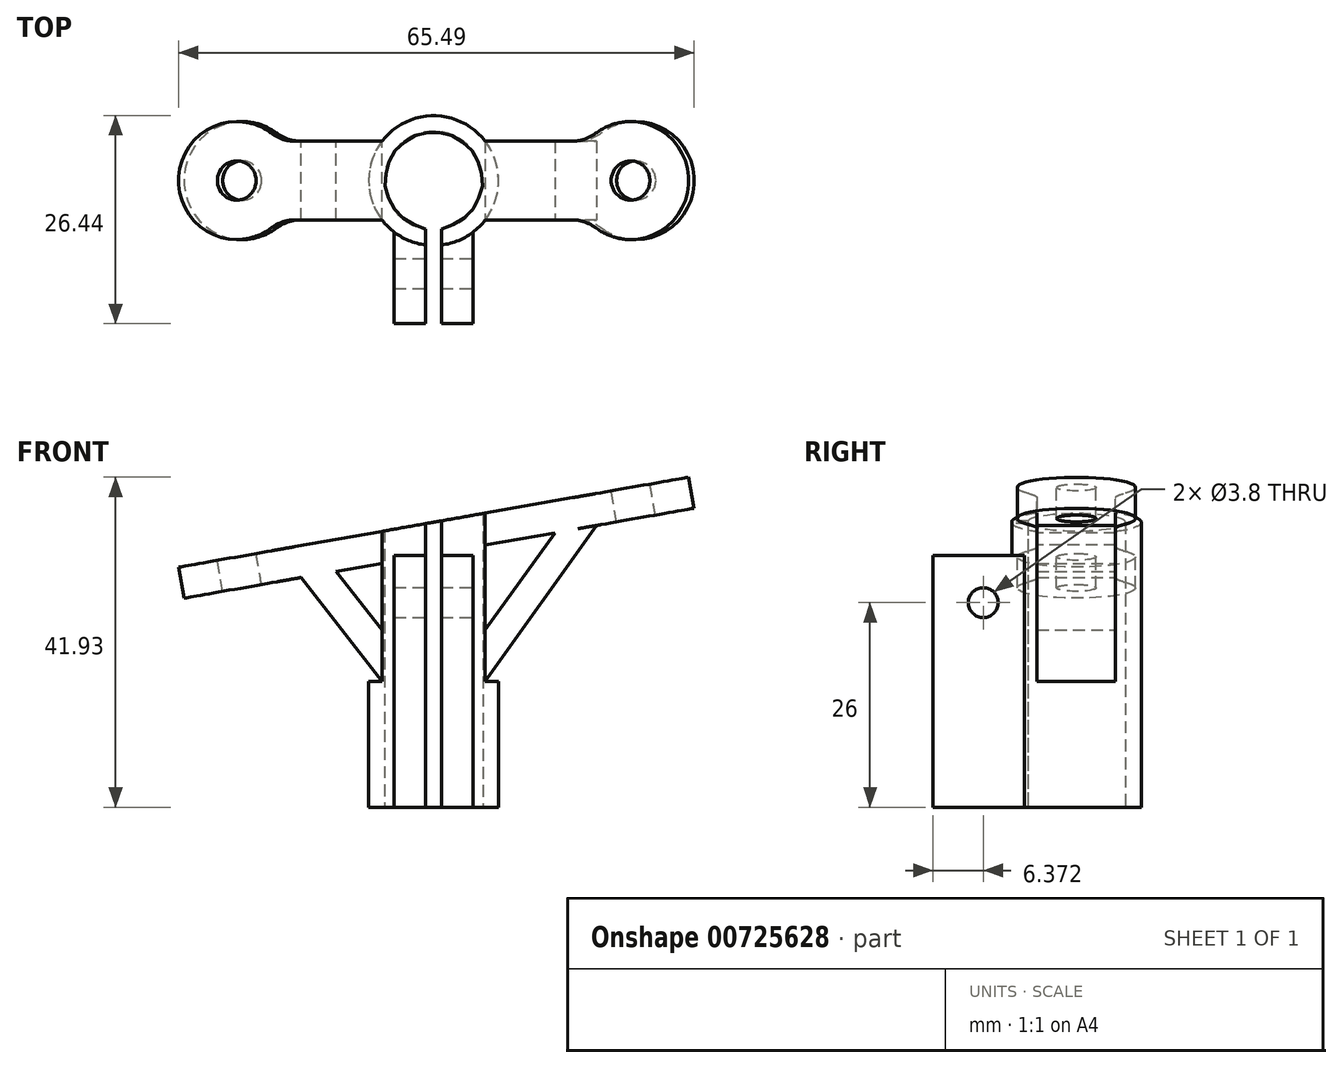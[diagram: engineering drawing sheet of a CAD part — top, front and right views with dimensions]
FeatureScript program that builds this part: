
annotation { "Feature Type Name" : "Feature", "Feature Type Description" : "" }
export const myFeature = defineFeature(function(context is Context, id is Id, definition is map)
    precondition{}
    {
        {
            var Q0;
            Q0=qCreatedBy(makeId("Top.planeOp"),FACE);
            var sketch = newSketch(context, id + "F0", { "sketchPlane" : qUnion([Q0])});
            skCircle(sketch, "E0", {"center": v(0, 0) * mm, "radius": 6.25 * mm});
            skCircle(sketch, "E1", {"center": v(0, 0) * mm, "radius": 8.25 * mm});
            skSolve(sketch);
        }
        {
            var Q0;
            Q0=makeQuery(id+"F0.imprint","IMPRINT",FACE,{"disambiguationData":[TD([[makeQuery(id+"F0.imprint","IMPRINT",EDGE,{"derivedFrom":sQuery(id+"F0.wireOp",EDGE,"E0")}),-1.0]])]});
            extrude(context, id + "F1", {"entities" : qUnion([Q0]), "depth" : 50 * mm, "offsetDistance" : 25 * mm});
        }
        {
            var Q0;
            Q0=makeQuery(id+"F0.imprint","IMPRINT",FACE,{"disambiguationData":[TD([[makeQuery(id+"F0.imprint","IMPRINT",EDGE,{"derivedFrom":sQuery(id+"F0.wireOp",EDGE,"E0")}),1.0]])]});
            var sketch = newSketch(context, id + "F2", { "sketchPlane" : qUnion([Q0])});
            skLineSegment(sketch, "E2", {"start": v(0, 0) * mm, "end": v(0, -8.02) * mm, "construction": true});
            skLineSegment(sketch, "E3", {"start": v(-1, -14.34) * mm, "end": v(-1, -4.34) * mm});
            skLineSegment(sketch, "E4.MirrorCS", {"start": v(1, -14.34) * mm, "end": v(1, -4.34) * mm});
            skLineSegment(sketch, "E5", {"start": v(-1, -14.34) * mm, "end": v(1, -14.34) * mm});
            skLineSegment(sketch, "E6", {"start": v(-1, -4.34) * mm, "end": v(1, -4.34) * mm});
            skCircle(sketch, "E7.0", {"center": v(0, 0) * mm, "radius": 6.25 * mm});
            skSolve(sketch);
        }
        {
            var Q0;
            {var subQ0=sQuery(id+"F2.wireOp",EDGE,"E5");Q0=makeQuery(id+"F2.imprint","IMPRINT",FACE,{"disambiguationData":[TD([[makeQuery(id+"F2.imprint","IMPRINT",EDGE,{"derivedFrom":subQ0}),1.0]])]});}
            extrude(context, id + "F3", {"entities" : qUnion([Q0]), "operationType" : NewBodyOperationType.REMOVE, "endBound" : BoundingType.THROUGH_ALL, "depth" : 25 * mm, "offsetDistance" : 25 * mm});
        }
        {
            var Q0;
            Q0=makeQuery(id+"F0.imprint","IMPRINT",FACE,{"disambiguationData":[TD([[makeQuery(id+"F0.imprint","IMPRINT",EDGE,{"derivedFrom":sQuery(id+"F0.wireOp",EDGE,"E0")}),-1.0]])]});
            var sketch = newSketch(context, id + "F4", { "sketchPlane" : qUnion([Q0])});
            skLineSegment(sketch, "E8.0", {"start": v(-1, -8.19) * mm, "end": v(-1, -6.17) * mm});
            skLineSegment(sketch, "E8.1", {"start": v(1, -8.19) * mm, "end": v(1, -6.17) * mm});
            skCircle(sketch, "E9.0", {"center": v(0, 0) * mm, "radius": 8.25 * mm});
            skLineSegment(sketch, "E10", {"start": v(-1, -8.19) * mm, "end": v(-1, -18.19) * mm});
            skLineSegment(sketch, "E11", {"start": v(-1, -18.19) * mm, "end": v(-5, -18.19) * mm});
            skLineSegment(sketch, "E12", {"start": v(-5, -18.19) * mm, "end": v(-5, -6.56) * mm});
            skLineSegment(sketch, "E13", {"start": v(0, 0) * mm, "end": v(0, -13.03) * mm, "construction": true});
            skLineSegment(sketch, "E14.MirrorCS", {"start": v(1, -8.19) * mm, "end": v(1, -18.19) * mm});
            skLineSegment(sketch, "E15.MirrorCS", {"start": v(5, -18.19) * mm, "end": v(5, -6.56) * mm});
            skLineSegment(sketch, "E16.MirrorCS", {"start": v(1, -18.19) * mm, "end": v(5, -18.19) * mm});
            skSolve(sketch);
        }
        {
            var Q0;
            {var subQ0=sQuery(id+"F4.wireOp",EDGE,"E10");Q0=makeQuery(id+"F4.imprint","IMPRINT",FACE,{"disambiguationData":[TD([[makeQuery(id+"F4.imprint","IMPRINT",EDGE,{"derivedFrom":subQ0}),-1.0]])]});}
            var Q1;
            {var subQ0=sQuery(id+"F4.wireOp",EDGE,"E14.MirrorCS");Q1=makeQuery(id+"F4.imprint","IMPRINT",FACE,{"disambiguationData":[TD([[makeQuery(id+"F4.imprint","IMPRINT",EDGE,{"derivedFrom":subQ0}),1.0]])]});}
            extrude(context, id + "F5", {"entities" : qUnion([Q0, Q1]), "operationType" : NewBodyOperationType.ADD, "depth" : 32 * mm, "offsetDistance" : 25 * mm});
        }
        {
            var Q0;
            Q0=makeQuery(id+"F5.opExtrude","SWEPT_FACE",FACE,{"disambiguationData":[OSD([sQuery(id+"F4.wireOp",EDGE,"E15.MirrorCS")])]});
            var sketch = newSketch(context, id + "F6", { "sketchPlane" : qUnion([Q0])});
            skPoint(sketch, "E17", {"position": v(-11.82, 26) * mm});
            skCircle(sketch, "E18", {"center": v(-11.82, 26) * mm, "radius": 1.9 * mm});
            skLineSegment(sketch, "E19.0", {"start": v(-8.25, 0) * mm, "end": v(8.25, 0) * mm});
            skLineSegment(sketch, "E20.0", {"start": v(-8.19, 50) * mm, "end": v(8.25, 50) * mm});
            skLineSegment(sketch, "E21", {"start": v(11.59, 26) * mm, "end": v(-11.82, 26) * mm, "construction": true});
            skLineSegment(sketch, "E22", {"start": v(0, 50) * mm, "end": v(0, 26) * mm, "construction": true});
            skSolve(sketch);
        }
        {
            var Q0;
            Q0=makeQuery(id+"F6.imprint","IMPRINT",FACE,{"disambiguationData":[TD([[makeQuery(id+"F6.imprint","IMPRINT",EDGE,{"derivedFrom":sQuery(id+"F6.wireOp",EDGE,"E18")}),1.0]])]});
            extrude(context, id + "F7", {"entities" : qUnion([Q0]), "operationType" : NewBodyOperationType.REMOVE, "endBound" : BoundingType.THROUGH_ALL, "oppositeDirection" : true, "depth" : 25 * mm, "offsetDistance" : 25 * mm});
        }
        {
            var Q0;
            Q0=qCreatedBy(makeId("Right.planeOp"),FACE);
            cPlane(context, id + "F8", {"entities" : qUnion([Q0]), "cplaneType" : CPlaneType.OFFSET, "offset" : 8.25 * mm, "width" : 150 * mm, "height" : 150 * mm});
        }
        {
            var Q0;
            Q0=qCreatedBy(id+"F8.planeOp",FACE);
            var sketch = newSketch(context, id + "F9", { "sketchPlane" : qUnion([Q0])});
            skPoint(sketch, "E23.0", {"position": v(-18.19, 16) * mm});
            skLineSegment(sketch, "E24", {"start": v(0, 16) * mm, "end": v(-5, 16) * mm, "construction": true});
            skLineSegment(sketch, "E25", {"start": v(-5, 35) * mm, "end": v(0, 35) * mm, "construction": true});
            skLineSegment(sketch, "E26.bottom", {"start": v(-5, 35) * mm, "end": v(5, 35) * mm, "construction": true});
            skLineSegment(sketch, "E26.top", {"start": v(-5, 16) * mm, "end": v(5, 16) * mm});
            skLineSegment(sketch, "E26.left", {"start": v(-5, 35) * mm, "end": v(-5, 16) * mm, "construction": true});
            skLineSegment(sketch, "E26.right", {"start": v(5, 35) * mm, "end": v(5, 16) * mm, "construction": true});
            skLineSegment(sketch, "E27.top", {"start": v(-5, 51) * mm, "end": v(5, 51) * mm});
            skLineSegment(sketch, "E27.left", {"start": v(-5, 16) * mm, "end": v(-5, 51) * mm});
            skLineSegment(sketch, "E27.right", {"start": v(5, 16) * mm, "end": v(5, 51) * mm});
            skSolve(sketch);
        }
        {
            var Q0;
            Q0=makeQuery(id+"F9.imprint","IMPRINT",FACE,{"disambiguationData":[TD([[makeQuery(id+"F9.imprint","IMPRINT",EDGE,{"derivedFrom":sQuery(id+"F9.wireOp",EDGE,"E26.top")}),1.0]])]});
            extrude(context, id + "F10", {"entities" : qUnion([Q0]), "operationType" : NewBodyOperationType.ADD, "depth" : 7.15 * mm, "offsetDistance" : 25 * mm, "hasSecondDirection" : true, "secondDirectionOppositeDirection" : true, "secondDirectionDepth" : 3.3 * mm, "hasSecondDirectionOffset" : true, "secondDirectionOffsetDistance" : 25 * mm});
        }
        {
            var Q0;
            Q0=qCreatedBy(makeId("Right.planeOp"),FACE);
            cPlane(context, id + "F11", {"entities" : qUnion([Q0]), "cplaneType" : CPlaneType.OFFSET, "offset" : 8.5 * mm, "oppositeDirection" : true, "width" : 150 * mm, "height" : 150 * mm});
        }
        {
            var Q0;
            Q0=qCreatedBy(id+"F11.planeOp",FACE);
            var sketch = newSketch(context, id + "F12", { "sketchPlane" : qUnion([Q0])});
            skLineSegment(sketch, "E28.0", {"start": v(-8.25, 0) * mm, "end": v(8.25, 0) * mm});
            skLineSegment(sketch, "E29", {"start": v(0, 0) * mm, "end": v(0, 35) * mm, "construction": true});
            skPoint(sketch, "E30.startSnap0", {"position": v(0, 17.5) * mm});
            skLineSegment(sketch, "E31.0", {"start": v(8.25, 35) * mm, "end": v(-8.19, 35) * mm});
            skLineSegment(sketch, "E32", {"start": v(5, 16) * mm, "end": v(5, 35) * mm, "construction": true});
            skLineSegment(sketch, "E33.MirrorCS", {"start": v(-5, 16) * mm, "end": v(-5, 35) * mm, "construction": true});
            skLineSegment(sketch, "E34.bottom", {"start": v(5, 35) * mm, "end": v(-5, 35) * mm});
            skLineSegment(sketch, "E34.top", {"start": v(5, 16) * mm, "end": v(-5, 16) * mm});
            skLineSegment(sketch, "E34.left", {"start": v(5, 35) * mm, "end": v(5, 16) * mm});
            skLineSegment(sketch, "E34.right", {"start": v(-5, 35) * mm, "end": v(-5, 16) * mm});
            skSolve(sketch);
        }
        {
            var Q0;
            Q0=makeQuery(id+"F12.imprint","IMPRINT",FACE,{"disambiguationData":[TD([[makeQuery(id+"F12.imprint","IMPRINT",EDGE,{"derivedFrom":sQuery(id+"F12.wireOp",EDGE,"E34.top")}),-1.0]])]});
            extrude(context, id + "F13", {"entities" : qUnion([Q0]), "operationType" : NewBodyOperationType.ADD, "oppositeDirection" : true, "depth" : 10 * mm, "offsetDistance" : 25 * mm, "hasSecondDirection" : true, "secondDirectionBound" : SecondDirectionBoundingType.UP_TO_NEXT, "secondDirectionOppositeDirection" : false, "secondDirectionDepth" : 25 * mm});
        }
        {
            var Q0;
            Q0=makeQuery(id+"F13.opExtrude","SWEPT_FACE",FACE,{"disambiguationData":[OSD([sQuery(id+"F12.wireOp",EDGE,"E34.left")])]});
            var sketch = newSketch(context, id + "F14", { "sketchPlane" : qUnion([Q0])});
            skLineSegment(sketch, "E35", {"start": v(18.5, 28.9) * mm, "end": v(6.56, 31) * mm});
            skLineSegment(sketch, "E36", {"start": v(6.56, 31) * mm, "end": v(6.56, 16) * mm});
            skPoint(sketch, "E37.0", {"position": v(0, 0) * mm});
            skLineSegment(sketch, "E38", {"start": v(0, 0) * mm, "end": v(0, 76.67) * mm, "construction": true});
            skLineSegment(sketch, "E39.MirrorCS", {"start": v(6.56, 22.5) * mm, "end": v(13.18, 31) * mm});
            skLineSegment(sketch, "E40.MirrorCS", {"start": v(18.25, 31) * mm, "end": v(6.56, 16) * mm});
            skLineSegment(sketch, "E41", {"start": v(12.53, 29.95) * mm, "end": v(14.37, 40.37) * mm, "construction": true});
            skLineSegment(sketch, "E42", {"start": v(13.23, 33.89) * mm, "end": v(22.74, 32.2) * mm, "construction": true});
            skLineSegment(sketch, "E43", {"start": v(18.5, 32.96) * mm, "end": v(6.91, 35) * mm});
            skLineSegment(sketch, "E44", {"start": v(18.5, 32.96) * mm, "end": v(17.8, 29.02) * mm});
            skLineSegment(sketch, "E45", {"start": v(17.8, 29.02) * mm, "end": v(18.5, 28.9) * mm, "construction": true});
            skLineSegment(sketch, "E46", {"start": v(18.5, 32.96) * mm, "end": v(18.5, 28.9) * mm});
            skLineSegment(sketch, "E47.0", {"start": v(-6.56, 50) * mm, "end": v(8.25, 50) * mm});
            skLineSegment(sketch, "E48", {"start": v(6.56, 35) * mm, "end": v(6.56, 50) * mm});
            skLineSegment(sketch, "E49", {"start": v(18.5, 47.92) * mm, "end": v(6.56, 47.92) * mm});
            skLineSegment(sketch, "E50", {"start": v(6.56, 47.92) * mm, "end": v(6.56, 35) * mm});
            skLineSegment(sketch, "E51", {"start": v(18.5, 47.92) * mm, "end": v(21.14, 47.92) * mm});
            skLineSegment(sketch, "E52", {"start": v(21.14, 47.92) * mm, "end": v(18.5, 32.96) * mm});
            skSolve(sketch);
        }
        {
            var Q0;
            {var subQ4=sQuery(id+"F14.wireOp",EDGE,"E39.MirrorCS");Q0=makeQuery(id+"F14.imprint","IMPRINT",FACE,{"disambiguationData":[TD([[makeQuery(id+"F14.imprint","IMPRINT",EDGE,{"derivedFrom":subQ4}),1.0]])]});}
            var Q1;
            {var subQ0=sQuery(id+"F12.wireOp",EDGE,"E34.left");var subQ1=sQuery(id+"F12.wireOp",EDGE,"E34.top");var subQ2=makeQuery(id+"F13.opExtrude","SWEPT_EDGE",EDGE,{"disambiguationData":[OSD([subQ1,subQ0])]});Q1=makeQuery(id+"F14.imprint","IMPRINT",FACE,{"disambiguationData":[TD([[makeQuery(id+"F14.imprint","IMPRINT",EDGE,{"derivedFrom":subQ2}),-1.0]])]});}
            var Q2;
            {var subQ0=sQuery(id+"F12.wireOp",EDGE,"E34.left");var subQ1=sQuery(id+"F12.wireOp",EDGE,"E34.top");var subQ2=makeQuery(id+"F13.opExtrude","SWEPT_EDGE",EDGE,{"disambiguationData":[OSD([subQ1,subQ0])]});Q2=makeQuery(id+"F14.imprint","IMPRINT",FACE,{"disambiguationData":[TD([[makeQuery(id+"F14.imprint","IMPRINT",EDGE,{"derivedFrom":subQ2}),-1.0]])]});}
            var Q3;
            {var subQ0=sQuery(id+"F14.wireOp",EDGE,"E43");Q3=makeQuery(id+"F14.imprint","IMPRINT",FACE,{"disambiguationData":[TD([[makeQuery(id+"F14.imprint","IMPRINT",EDGE,{"derivedFrom":subQ0}),-1.0]])]});}
            var Q4;
            {var subQ0=sQuery(id+"F14.wireOp",EDGE,"E46");Q4=makeQuery(id+"F14.imprint","IMPRINT",FACE,{"disambiguationData":[TD([[makeQuery(id+"F14.imprint","IMPRINT",EDGE,{"derivedFrom":subQ0}),-1.0]])]});}
            extrude(context, id + "F15", {"entities" : qUnion([Q0, Q1, Q2, Q3, Q4]), "operationType" : NewBodyOperationType.REMOVE, "endBound" : BoundingType.THROUGH_ALL, "oppositeDirection" : true, "depth" : 25 * mm, "offsetDistance" : 25 * mm});
        }
        {
            var Q0;
            Q0=makeQuery(id+"F15.boolean.opBoolean","COPY",FACE,{"derivedFrom":makeQuery(id+"F15.opExtrude","SWEPT_FACE",FACE,{"disambiguationData":[OSD([sQuery(id+"F14.wireOp",EDGE,"E44")])]})});
            extrude(context, id + "F16", {"entities" : qUnion([Q0]), "operationType" : NewBodyOperationType.ADD, "depth" : 7.15 * mm, "offsetDistance" : 25 * mm});
        }
        {
            var Q0;
            Q0=makeQuery(id+"F0.imprint","IMPRINT",FACE,{"disambiguationData":[TD([[makeQuery(id+"F0.imprint","IMPRINT",EDGE,{"derivedFrom":sQuery(id+"F0.wireOp",EDGE,"E0")}),1.0]])]});
            extrude(context, id + "F17", {"entities" : qUnion([Q0]), "operationType" : NewBodyOperationType.REMOVE, "endBound" : BoundingType.THROUGH_ALL, "depth" : 25 * mm, "offsetDistance" : 25 * mm});
        }
        {
            var Q0;
            Q0=makeQuery(id+"F10.opExtrude","SWEPT_FACE",FACE,{"disambiguationData":[OSD([sQuery(id+"F9.wireOp",EDGE,"E27.left")])]});
            var sketch = newSketch(context, id + "F18", { "sketchPlane" : qUnion([Q0])});
            skLineSegment(sketch, "E53.0", {"start": v(-6.56, 31) * mm, "end": v(-12.38, 29.97) * mm});
            skLineSegment(sketch, "E54", {"start": v(-6.56, 31) * mm, "end": v(39.32, 39.09) * mm});
            skLineSegment(sketch, "E55.0", {"start": v(-6.56, 16) * mm, "end": v(-16.84, 29.19) * mm});
            skLineSegment(sketch, "E55.1", {"start": v(-12.38, 29.97) * mm, "end": v(-6.56, 22.5) * mm});
            skPoint(sketch, "E56.0", {"position": v(0, 0) * mm});
            skLineSegment(sketch, "E57", {"start": v(0, 0) * mm, "end": v(0, 45.46) * mm, "construction": true});
            skLineSegment(sketch, "E58", {"start": v(6.56, 22.5) * mm, "end": v(15.4, 34.87) * mm});
            skLineSegment(sketch, "E59", {"start": v(6.56, 16) * mm, "end": v(20.72, 35.81) * mm});
            skLineSegment(sketch, "E60.0", {"start": v(6.56, 16) * mm, "end": v(6.56, 37.38) * mm});
            skLineSegment(sketch, "E61", {"start": v(6.56, 33.31) * mm, "end": v(15.4, 34.87) * mm});
            skSolve(sketch);
        }
        {
            var Q0;
            {var subQ0=sQuery(id+"F18.wireOp",EDGE,"E59");Q0=makeQuery(id+"F18.imprint","IMPRINT",FACE,{"disambiguationData":[TD([[makeQuery(id+"F18.imprint","IMPRINT",EDGE,{"derivedFrom":subQ0}),-1.0]])]});}
            var Q1;
            {var subQ0=sQuery(id+"F18.wireOp",EDGE,"E58");Q1=makeQuery(id+"F18.imprint","IMPRINT",FACE,{"disambiguationData":[TD([[makeQuery(id+"F18.imprint","IMPRINT",EDGE,{"derivedFrom":subQ0}),1.0]])]});}
            extrude(context, id + "F19", {"entities" : qUnion([Q0, Q1]), "operationType" : NewBodyOperationType.REMOVE, "depth" : 25 * mm, "offsetDistance" : 25 * mm});
        }
        {
            var Q0;
            Q0=makeQuery(id+"F10.opExtrude","CAP_FACE",FACE,{"disambiguationData":[OSD([sQuery(id+"F9.wireOp",EDGE,"E26.top"),sQuery(id+"F9.wireOp",EDGE,"E27.top"),sQuery(id+"F9.wireOp",EDGE,"E27.left"),sQuery(id+"F9.wireOp",EDGE,"E27.right")])],"isStart":false});
            extrude(context, id + "F20", {"entities" : qUnion([Q0]), "operationType" : NewBodyOperationType.ADD, "depth" : 10 * mm, "offsetDistance" : 25 * mm});
        }
        {
            var Q0;
            {var subQ0=sQuery(id+"F18.wireOp",EDGE,"E58");Q0=makeQuery(id+"F18.imprint","IMPRINT",FACE,{"disambiguationData":[TD([[makeQuery(id+"F18.imprint","IMPRINT",EDGE,{"derivedFrom":subQ0}),1.0]])]});}
            extrude(context, id + "F21", {"entities" : qUnion([Q0]), "operationType" : NewBodyOperationType.REMOVE, "oppositeDirection" : true, "depth" : 25 * mm, "offsetDistance" : 25 * mm});
        }
        {
            var Q0;
            {var subQ0=sQuery(id+"F9.wireOp",EDGE,"E27.left");Q0=makeQuery(id+"F20.boolean.opBoolean","MERGE",FACE,{"derivedFrom":[makeQuery(id+"F10.opExtrude","SWEPT_FACE",FACE,{"disambiguationData":[OSD([subQ0])]}),makeQuery(id+"F20.opExtrude","SWEPT_FACE",FACE,{"disambiguationData":[OSD([subQ0])]})]});}
            var sketch = newSketch(context, id + "F22", { "sketchPlane" : qUnion([Q0])});
            skLineSegment(sketch, "E62.0", {"start": v(-6.56, 31) * mm, "end": v(39.32, 39.09) * mm});
            skLineSegment(sketch, "E62.1", {"start": v(6.56, 16) * mm, "end": v(20.72, 35.81) * mm});
            skSolve(sketch);
        }
        {
            var Q0;
            {var subQ0=sQuery(id+"F22.wireOp",EDGE,"E62.1");Q0=makeQuery(id+"F22.imprint","IMPRINT",FACE,{"disambiguationData":[TD([[makeQuery(id+"F22.imprint","IMPRINT",EDGE,{"derivedFrom":subQ0}),-1.0]])]});}
            extrude(context, id + "F23", {"entities" : qUnion([Q0]), "operationType" : NewBodyOperationType.REMOVE, "endBound" : BoundingType.THROUGH_ALL, "oppositeDirection" : true, "depth" : 25 * mm, "offsetDistance" : 25 * mm});
        }
        {
            var Q0;
            {var subQ5=sQuery(id+"F14.wireOp",EDGE,"E49");Q0=makeQuery(id+"F14.imprint","IMPRINT",FACE,{"disambiguationData":[TD([[makeQuery(id+"F14.imprint","IMPRINT",EDGE,{"derivedFrom":subQ5}),1.0]])]});}
            var Q1;
            {var subQ0=sQuery(id+"F14.wireOp",EDGE,"E43");Q1=makeQuery(id+"F14.imprint","IMPRINT",FACE,{"disambiguationData":[TD([[makeQuery(id+"F14.imprint","IMPRINT",EDGE,{"derivedFrom":subQ0}),-1.0]])]});}
            extrude(context, id + "F24", {"entities" : qUnion([Q0, Q1]), "operationType" : NewBodyOperationType.ADD, "depth" : 25 * mm, "offsetDistance" : 25 * mm, "hasSecondDirection" : true, "secondDirectionOppositeDirection" : true, "secondDirectionDepth" : 25 * mm});
        }
        {
            var Q0;
            Q0=makeQuery(id+"F24.opExtrude","SWEPT_FACE",FACE,{"disambiguationData":[OSD([sQuery(id+"F14.wireOp",EDGE,"E52")])]});
            extrude(context, id + "F25", {"entities" : qUnion([Q0]), "operationType" : NewBodyOperationType.REMOVE, "endBound" : BoundingType.THROUGH_ALL, "oppositeDirection" : true, "depth" : 25 * mm, "offsetDistance" : 25 * mm});
        }
        {
            var Q0;
            {var subQ1=sQuery(id+"F12.wireOp",EDGE,"E34.left");var subQ3=sQuery(id+"F12.wireOp",EDGE,"E31.0");Q0=makeQuery(id+"F24.boolean.opBoolean","SPLIT",FACE,{"disambiguationData":[TD([makeQuery(id+"F13.opExtrude","SWEPT_FACE",FACE,{"disambiguationData":[OSD([subQ1])]})])],"derivedFrom":makeQuery(id+"F24.opExtrude","SWEPT_FACE",FACE,{"disambiguationData":[OSD([subQ3,subQ1])]})});}
            var Q1;
            {var subQ1=sQuery(id+"F12.wireOp",EDGE,"E34.right");var subQ3=sQuery(id+"F12.wireOp",EDGE,"E34.left");var subQ4=sQuery(id+"F12.wireOp",EDGE,"E31.0");Q1=makeQuery(id+"F24.boolean.opBoolean","SPLIT",FACE,{"disambiguationData":[TD([makeQuery(id+"F13.opExtrude","SWEPT_FACE",FACE,{"disambiguationData":[OSD([subQ1])]})])],"derivedFrom":makeQuery(id+"F24.opExtrude","SWEPT_FACE",FACE,{"disambiguationData":[OSD([subQ4,subQ3])]})});}
            extrude(context, id + "F26", {"entities" : qUnion([Q0, Q1]), "operationType" : NewBodyOperationType.REMOVE, "oppositeDirection" : true, "depth" : 25 * mm, "offsetDistance" : 25 * mm});
        }
        {
            var Q0;
            {var subQ0=sQuery(id+"F14.wireOp",EDGE,"E52");var subQ1=sQuery(id+"F14.wireOp",EDGE,"E46");var subQ2=sQuery(id+"F14.wireOp",EDGE,"E44");var subQ3=sQuery(id+"F14.wireOp",EDGE,"E43");var subQ4=sQuery(id+"F12.wireOp",EDGE,"E34.left");Q0=makeQuery(id+"F25.boolean.opBoolean","MERGE",FACE,{"derivedFrom":[makeQuery(id+"F16.boolean.opBoolean","MERGE",FACE,{"derivedFrom":[makeQuery(id+"F15.boolean.opBoolean","COPY",FACE,{"derivedFrom":makeQuery(id+"F15.opExtrude","SWEPT_FACE",FACE,{"disambiguationData":[OSD([subQ3])]})}),makeQuery(id+"F16.opExtrude","SWEPT_FACE",FACE,{"disambiguationData":[OSD([subQ4,subQ3,subQ2,subQ1,subQ0])]})]})],"fromTools":[makeQuery(id+"F25.opExtrude","SWEPT_FACE",FACE,{"disambiguationData":[OSD([subQ4,subQ3,subQ2,subQ1,subQ0])]})]});}
            var sketch = newSketch(context, id + "F27", { "sketchPlane" : qUnion([Q0])});
            skLineSegment(sketch, "E63", {"start": v(6.29, 0) * mm, "end": v(6.29, 33.4) * mm, "construction": true});
            skPoint(sketch, "E64", {"position": v(31.69, 0) * mm});
            skPoint(sketch, "E65.MirrorP", {"position": v(-19.11, 0) * mm});
            skCircle(sketch, "E66", {"center": v(-19.11, 0) * mm, "radius": 7.5 * mm});
            skCircle(sketch, "E67.MirrorC", {"center": v(31.69, 0) * mm, "radius": 7.5 * mm});
            skSolve(sketch);
        }
        {
            var Q0;
            {var subQ1=sQuery(id+"F12.wireOp",EDGE,"E34.left");var subQ3=sQuery(id+"F14.wireOp",EDGE,"E52");var subQ4=sQuery(id+"F14.wireOp",EDGE,"E46");var subQ5=sQuery(id+"F14.wireOp",EDGE,"E44");var subQ6=sQuery(id+"F14.wireOp",EDGE,"E43");var subQ12=makeQuery(id+"F16.opExtrude","CAP_EDGE",EDGE,{"disambiguationData":[OSD([subQ1,subQ6,subQ5,subQ4,subQ3])],"isStart":false});Q0=makeQuery(id+"F27.imprint","IMPRINT",FACE,{"disambiguationData":[TD([[makeQuery(id+"F27.imprint","IMPRINT",EDGE,{"derivedFrom":subQ12}),-1.0]])]});}
            var Q1;
            {var subQ1=sQuery(id+"F12.wireOp",EDGE,"E34.left");var subQ3=sQuery(id+"F14.wireOp",EDGE,"E52");var subQ4=sQuery(id+"F14.wireOp",EDGE,"E46");var subQ5=sQuery(id+"F14.wireOp",EDGE,"E44");var subQ6=sQuery(id+"F14.wireOp",EDGE,"E43");var subQ12=makeQuery(id+"F16.opExtrude","CAP_EDGE",EDGE,{"disambiguationData":[OSD([subQ1,subQ6,subQ5,subQ4,subQ3])],"isStart":false});Q1=makeQuery(id+"F27.imprint","IMPRINT",FACE,{"disambiguationData":[TD([[makeQuery(id+"F27.imprint","IMPRINT",EDGE,{"derivedFrom":subQ12}),1.0]])]});}
            var Q2;
            {var subQ1=makeQuery(id+"F25.opExtrude","SWEPT_FACE",FACE,{"disambiguationData":[OSD([sQuery(id+"F12.wireOp",EDGE,"E34.left"),sQuery(id+"F14.wireOp",EDGE,"E43"),sQuery(id+"F14.wireOp",EDGE,"E44"),sQuery(id+"F14.wireOp",EDGE,"E46"),sQuery(id+"F14.wireOp",EDGE,"E52")])]});var subQ2=sQuery(id+"F9.wireOp",EDGE,"E27.right");var subQ5=sQuery(id+"F9.wireOp",EDGE,"E27.left");var subQ8=makeQuery(id+"F25.boolean.opBoolean","INTERSECT",EDGE,{"derivedFrom":[makeQuery(id+"F20.opExtrude","CAP_FACE",FACE,{"disambiguationData":[OSD([sQuery(id+"F9.wireOp",EDGE,"E26.top"),sQuery(id+"F9.wireOp",EDGE,"E27.top"),subQ5,subQ2])],"isStart":false}),subQ1]});Q2=makeQuery(id+"F27.imprint","IMPRINT",FACE,{"disambiguationData":[TD([[makeQuery(id+"F27.imprint","IMPRINT",EDGE,{"derivedFrom":subQ8}),1.0]])]});}
            var Q3;
            {var subQ1=makeQuery(id+"F25.opExtrude","SWEPT_FACE",FACE,{"disambiguationData":[OSD([sQuery(id+"F12.wireOp",EDGE,"E34.left"),sQuery(id+"F14.wireOp",EDGE,"E43"),sQuery(id+"F14.wireOp",EDGE,"E44"),sQuery(id+"F14.wireOp",EDGE,"E46"),sQuery(id+"F14.wireOp",EDGE,"E52")])]});var subQ2=sQuery(id+"F9.wireOp",EDGE,"E27.right");var subQ5=sQuery(id+"F9.wireOp",EDGE,"E27.left");var subQ8=makeQuery(id+"F25.boolean.opBoolean","INTERSECT",EDGE,{"derivedFrom":[makeQuery(id+"F20.opExtrude","CAP_FACE",FACE,{"disambiguationData":[OSD([sQuery(id+"F9.wireOp",EDGE,"E26.top"),sQuery(id+"F9.wireOp",EDGE,"E27.top"),subQ5,subQ2])],"isStart":false}),subQ1]});Q3=makeQuery(id+"F27.imprint","IMPRINT",FACE,{"disambiguationData":[TD([[makeQuery(id+"F27.imprint","IMPRINT",EDGE,{"derivedFrom":subQ8}),-1.0]])]});}
            var Q4;
            {var subQ0=sQuery(id+"F14.wireOp",EDGE,"E44");var subQ1=sQuery(id+"F14.wireOp",EDGE,"E35");Q4=makeQuery(id+"F16.boolean.opBoolean","MERGE",FACE,{"derivedFrom":[makeQuery(id+"F15.boolean.opBoolean","COPY",FACE,{"derivedFrom":makeQuery(id+"F15.opExtrude","SWEPT_FACE",FACE,{"disambiguationData":[OSD([subQ1]),TDD([makeQuery(id+"F14.imprint","IMPRINT",EDGE,{"disambiguationData":[TD([[makeQuery(id+"F14.imprint","INTERSECT",VERTEX,{"derivedFrom":[subQ1,subQ0]}),-1.0]])],"derivedFrom":subQ1})])]})}),makeQuery(id+"F16.opExtrude","SWEPT_FACE",FACE,{"disambiguationData":[OSD([subQ1,subQ0])]})]});}
            extrude(context, id + "F28", {"entities" : qUnion([Q0, Q1, Q2, Q3]), "operationType" : NewBodyOperationType.ADD, "endBound" : BoundingType.UP_TO_SURFACE, "oppositeDirection" : true, "depth" : 25 * mm, "endBoundEntityFace" : qUnion([Q4]), "offsetDistance" : 25 * mm});
        }
        {
            var Q0;
            {var subQ0=sQuery(id+"F12.wireOp",EDGE,"E34.left");var subQ1=sQuery(id+"F12.wireOp",EDGE,"E31.0");Q0=makeQuery(id+"F28.boolean.opBoolean","INTERSECT",EDGE,{"derivedFrom":[makeQuery(id+"F26.boolean.opBoolean","MERGE",FACE,{"derivedFrom":[makeQuery(id+"F16.boolean.opBoolean","MERGE",FACE,{"derivedFrom":[makeQuery(id+"F13.opExtrude","SWEPT_FACE",FACE,{"disambiguationData":[OSD([subQ0])]}),makeQuery(id+"F16.opExtrude","SWEPT_FACE",FACE,{"disambiguationData":[OSD([sQuery(id+"F14.wireOp",EDGE,"E44")])]})]})],"fromTools":[makeQuery(id+"F26.opExtrude","SWEPT_FACE",FACE,{"disambiguationData":[OSD([subQ1,subQ0]),TDD([makeQuery(id+"F13.opExtrude","SWEPT_EDGE",EDGE,{"disambiguationData":[OSD([subQ1,subQ0])]})])]})]}),makeQuery(id+"F28.opExtrude","SWEPT_FACE",FACE,{"disambiguationData":[OSD([sQuery(id+"F27.wireOp",EDGE,"E66")])]})]});}
            var Q1;
            {var subQ0=sQuery(id+"F9.wireOp",EDGE,"E27.right");Q1=makeQuery(id+"F28.boolean.opBoolean","INTERSECT",EDGE,{"derivedFrom":[makeQuery(id+"F20.boolean.opBoolean","MERGE",FACE,{"derivedFrom":[makeQuery(id+"F10.opExtrude","SWEPT_FACE",FACE,{"disambiguationData":[OSD([subQ0])]}),makeQuery(id+"F20.opExtrude","SWEPT_FACE",FACE,{"disambiguationData":[OSD([subQ0])]})]}),makeQuery(id+"F28.opExtrude","SWEPT_FACE",FACE,{"disambiguationData":[OSD([sQuery(id+"F27.wireOp",EDGE,"E67.MirrorC")])]})]});}
            var Q2;
            {var subQ0=sQuery(id+"F9.wireOp",EDGE,"E27.left");Q2=makeQuery(id+"F28.boolean.opBoolean","INTERSECT",EDGE,{"derivedFrom":[makeQuery(id+"F20.boolean.opBoolean","MERGE",FACE,{"derivedFrom":[makeQuery(id+"F10.opExtrude","SWEPT_FACE",FACE,{"disambiguationData":[OSD([subQ0])]}),makeQuery(id+"F20.opExtrude","SWEPT_FACE",FACE,{"disambiguationData":[OSD([subQ0])]})]}),makeQuery(id+"F28.opExtrude","SWEPT_FACE",FACE,{"disambiguationData":[OSD([sQuery(id+"F27.wireOp",EDGE,"E67.MirrorC")])]})]});}
            var Q3;
            {var subQ0=sQuery(id+"F12.wireOp",EDGE,"E34.right");Q3=makeQuery(id+"F28.boolean.opBoolean","INTERSECT",EDGE,{"derivedFrom":[makeQuery(id+"F26.boolean.opBoolean","MERGE",FACE,{"derivedFrom":[makeQuery(id+"F16.boolean.opBoolean","MERGE",FACE,{"derivedFrom":[makeQuery(id+"F13.opExtrude","SWEPT_FACE",FACE,{"disambiguationData":[OSD([subQ0])]}),makeQuery(id+"F16.opExtrude","SWEPT_FACE",FACE,{"disambiguationData":[OSD([subQ0,sQuery(id+"F14.wireOp",EDGE,"E44")])]})]})],"fromTools":[makeQuery(id+"F26.opExtrude","SWEPT_FACE",FACE,{"disambiguationData":[OSD([sQuery(id+"F12.wireOp",EDGE,"E31.0"),subQ0])]})]}),makeQuery(id+"F28.opExtrude","SWEPT_FACE",FACE,{"disambiguationData":[OSD([sQuery(id+"F27.wireOp",EDGE,"E66")])]})]});}
            fillet(context, id + "F29", {"entities" : qUnion([Q0, Q1, Q2, Q3]), "radius" : 5 * mm, "tangentPropagation" : true, "allowEdgeOverflow" : false});
        }
        {
            var Q0;
            {var subQ0=sQuery(id+"F14.wireOp",EDGE,"E52");var subQ1=sQuery(id+"F14.wireOp",EDGE,"E46");var subQ2=sQuery(id+"F14.wireOp",EDGE,"E44");var subQ3=sQuery(id+"F14.wireOp",EDGE,"E43");var subQ4=sQuery(id+"F12.wireOp",EDGE,"E34.left");Q0=makeQuery(id+"F28.boolean.opBoolean","MERGE",FACE,{"derivedFrom":[makeQuery(id+"F25.boolean.opBoolean","MERGE",FACE,{"derivedFrom":[makeQuery(id+"F16.boolean.opBoolean","MERGE",FACE,{"derivedFrom":[makeQuery(id+"F15.boolean.opBoolean","COPY",FACE,{"derivedFrom":makeQuery(id+"F15.opExtrude","SWEPT_FACE",FACE,{"disambiguationData":[OSD([subQ3])]})}),makeQuery(id+"F16.opExtrude","SWEPT_FACE",FACE,{"disambiguationData":[OSD([subQ4,subQ3,subQ2,subQ1,subQ0])]})]})],"fromTools":[makeQuery(id+"F25.opExtrude","SWEPT_FACE",FACE,{"disambiguationData":[OSD([subQ4,subQ3,subQ2,subQ1,subQ0])]})]}),makeQuery(id+"F28.opExtrude","CAP_FACE",FACE,{"disambiguationData":[OSD([sQuery(id+"F27.wireOp",EDGE,"E66")])],"isStart":true}),makeQuery(id+"F28.opExtrude","CAP_FACE",FACE,{"disambiguationData":[OSD([sQuery(id+"F27.wireOp",EDGE,"E67.MirrorC")])],"isStart":true})]});}
            var sketch = newSketch(context, id + "F30", { "sketchPlane" : qUnion([Q0])});
            skArc(sketch, "E68.0", {"start": v(27.19, 6) * mm, "mid": v(39.19, 0) * mm, "end": v(27.19, -6) * mm});
            skArc(sketch, "E69.0", {"start": v(-14.61, 6) * mm, "mid": v(-26.61, 0) * mm, "end": v(-14.61, -6) * mm});
            skCircle(sketch, "E70", {"center": v(31.69, 0) * mm, "radius": 2.5 * mm});
            skCircle(sketch, "E71", {"center": v(-19.11, 0) * mm, "radius": 2.5 * mm});
            skSolve(sketch);
        }
        {
            var Q0;
            Q0=makeQuery(id+"F30.imprint","IMPRINT",FACE,{"disambiguationData":[TD([[makeQuery(id+"F30.imprint","IMPRINT",EDGE,{"derivedFrom":sQuery(id+"F30.wireOp",EDGE,"E70")}),1.0]])]});
            var Q1;
            Q1=makeQuery(id+"F30.imprint","IMPRINT",FACE,{"disambiguationData":[TD([[makeQuery(id+"F30.imprint","IMPRINT",EDGE,{"derivedFrom":sQuery(id+"F30.wireOp",EDGE,"E71")}),1.0]])]});
            extrude(context, id + "F31", {"entities" : qUnion([Q0, Q1]), "operationType" : NewBodyOperationType.REMOVE, "oppositeDirection" : true, "depth" : 25 * mm, "offsetDistance" : 25 * mm});
        }
    });
